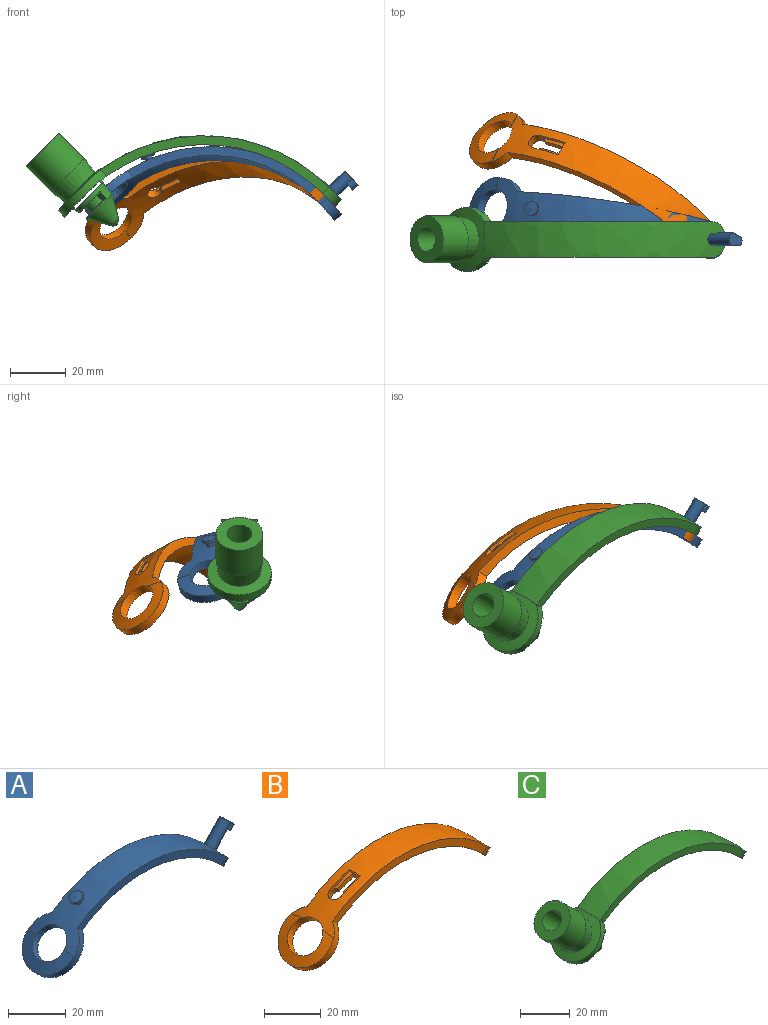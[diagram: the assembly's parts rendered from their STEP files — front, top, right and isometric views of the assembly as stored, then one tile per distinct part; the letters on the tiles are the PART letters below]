
ASSEMBLY  parts=3 mates=1
PART A: 20 faces, bbox 97.4x31.8x29.1 mm
  f0: sphere r=56.9mm, area 1169.8mm2, adj f1,f2,f3,f4,f9,f10,f11,f12
  f1: plane 72.67x18.82mm, normal (0,1,0), area 245.3mm2, adj f0,f8,f9,f11
  f2: plane 72.67x18.82mm, normal (0,-1,0), area 245.3mm2, adj f0,f8,f9,f11
  f3: cone r=40.93mm half-angle=46deg, axis (-1,0,0), area 1.2mm2, adj f0,f5,f9,f10
  f4: cone r=40.93mm half-angle=46deg, axis (-1,0,0), area 1.2mm2, adj f0,f5,f9,f10
  f5: sphere r=57.15mm, area 135.1mm2, adj f3,f4,f9,f10
  f6: sphere r=53.98mm, area 247.2mm2, adj f7,f9,f10
  f7: cone r=43.67mm half-angle=54deg, axis (-1,0,0), area 4.2mm2, adj f6,f8,f9
  f8: sphere r=53.72mm, area 1032.4mm2, adj f1,f2,f7,f9,f11
  f9: cylinder r=11.43mm len=22.86mm, axis (0.71,0,-0.71), area 184.7mm2, adj f0,f1,f2,f3,f4,f5,f6,f7
  f10: cone r=6.43mm half-angle=6.9deg, axis (-0.71,0,0.71), area 128.2mm2, adj f0,f3,f4,f5,f6
  f11: cylinder r=6.35mm len=12.7mm, axis (-0.71,0,-0.71), area 63.8mm2, adj f0,f1,f2,f8
  f12: cylinder r=2.28mm len=11.12mm, axis (0.68,0,0.73), area 149.3mm2, adj f0,f13,f14,f15
  f13: plane 5x4.69mm, normal (0.68,0,0.73), area 23.8mm2, adj f12,f14
  f14: cylinder r=1.78mm len=3.78mm, axis (0.68,0,0.73), area 19.8mm2, adj f12,f13,f15
  f15: plane 3.56x2.05mm, normal (-0.68,0,-0.73), area 7.4mm2, adj f12,f14
  f16: plane 5.08x4.53mm, normal (0.45,0,-0.89), area 15.2mm2, adj f17,f19
  f17: cylinder r=1.27mm len=3.13mm, axis (-0.45,0,0.89), area 15.3mm2, adj f0,f16
  f18: cone r=2.54mm half-angle=85deg, axis (0.45,0,-0.89), area 20.3mm2, adj f19
  f19: cylinder r=2.54mm len=5.08mm, axis (-0.45,0,0.89), area 16.7mm2, adj f16,f18
PART B: 21 faces, bbox 96.8x31.8x29.9 mm
  f0: sphere r=56.9mm, area 1144.5mm2, adj f2,f3,f6,f7,f8,f9,f14,f15
  f1: sphere r=60.07mm, area 1134.9mm2, adj f6,f7,f11,f12,f14,f15,f16,f17
  f2: plane 7.97x4.53mm, normal (0,1,0), area 14.9mm2, adj f0,f4,f17,f20
  f3: plane 7.97x4.53mm, normal (0,-1,0), area 14.9mm2, adj f0,f5,f17,f20
  f4: cylinder r=58.8mm len=9.51mm, axis (0,-1,0), area 10.9mm2, adj f2,f17,f19,f20
  f5: cylinder r=58.8mm len=9.51mm, axis (0,-1,0), area 10.9mm2, adj f3,f17,f18,f20
  f6: plane 77.22x19.75mm, normal (0,1,0), area 261.2mm2, adj f0,f1,f14,f16
  f7: plane 77.22x19.75mm, normal (0,-1,0), area 261.2mm2, adj f0,f1,f14,f16
  f8: cone r=40.93mm half-angle=46deg, axis (-1,0,0), area 1.2mm2, adj f0,f10,f14,f15
  f9: cone r=40.93mm half-angle=46deg, axis (-1,0,0), area 1.2mm2, adj f0,f10,f14,f15
  f10: sphere r=57.15mm, area 135.1mm2, adj f8,f9,f14,f15
  f11: cone r=46.21mm half-angle=50deg, axis (-1,0,0), area 1.4mm2, adj f1,f13,f14,f15
  f12: cone r=46.21mm half-angle=50deg, axis (-1,0,0), area 1.4mm2, adj f1,f13,f14,f15
  f13: sphere r=60.32mm, area 166.4mm2, adj f11,f12,f14,f15
  f14: cylinder r=11.43mm len=22.86mm, axis (0.71,0,-0.71), area 191.3mm2, adj f0,f1,f6,f7,f8,f9,f10,f11
  f15: cone r=6.43mm half-angle=6.9deg, axis (-0.71,0,0.71), area 143.2mm2, adj f0,f1,f8,f9,f10,f11,f12,f13
  f16: cylinder r=6.35mm len=12.7mm, axis (-0.71,0,-0.71), area 63.7mm2, adj f0,f1,f6,f7
  f17: plane 5.6x3.07mm, normal (-0.96,0,-0.29), area 12.8mm2, adj f0,f1,f2,f3,f4,f5,f18,f19
  f18: plane 10.08x5.01mm, normal (0,-1,0), area 12.5mm2, adj f1,f5,f17,f20
  f19: plane 10.08x5.01mm, normal (0,1,0), area 12.5mm2, adj f1,f4,f17,f20
  f20: cylinder r=2.79mm len=6.02mm, axis (0.45,0,-0.89), area 38.7mm2, adj f0,f1,f2,f3,f4,f5,f18,f19
PART C: 36 faces, bbox 112.8x26.4x33.2 mm
  f0: sphere r=60.07mm, area 1159.1mm2, adj f1,f2,f6,f9,f10,f11,f26,f27
  f1: cone r=6.43mm half-angle=6.9deg, axis (-0.71,0,0.71), area 134.6mm2, adj f0,f2,f3,f4,f5,f17,f21,f24
  f2: cone r=6.43mm half-angle=6.9deg, axis (-0.71,0,0.71), area 0.2mm2, adj f0,f1,f33
  f3: cone r=46.21mm half-angle=50deg, axis (-1,0,0), area 0.2mm2, adj f1,f5,f30
  f4: cone r=46.21mm half-angle=50deg, axis (-1,0,0), area 0.2mm2, adj f1,f5,f30
  f5: sphere r=60.32mm, area 100.4mm2, adj f1,f3,f4,f6,f29,f30,f32
  f6: cylinder r=11.43mm len=22.86mm, axis (0.71,0,-0.71), area 177.8mm2, adj f0,f5,f10,f11,f13,f29,f30,f32
  f7: cone r=3.13mm half-angle=3.1deg, axis (-0.71,0,0.71), area 530mm2, adj f14,f30
  f8: sphere r=63.25mm, area 1174.1mm2, adj f9,f10,f11,f12,f26,f27
  f9: cylinder r=2.28mm len=5mm, axis (0.73,0,0.68), area 34mm2, adj f0,f8,f27
  f10: plane 81.94x20.69mm, normal (0,1,0), area 277.1mm2, adj f0,f6,f8,f12,f13,f26
  f11: plane 81.94x20.69mm, normal (0,-1,0), area 277.1mm2, adj f0,f6,f8,f12,f13,f26
  f12: cone r=51.37mm half-angle=54deg, axis (-1,0,0), area 3.2mm2, adj f8,f10,f11,f13
  f13: sphere r=63.5mm, area 217.3mm2, adj f6,f10,f11,f12,f16
  f14: plane 16.76x11.85mm, normal (-0.71,0,0.71), area 160.1mm2, adj f7,f15
  f15: cylinder r=8.38mm len=20.83mm, axis (0.71,0,-0.71), area 668.9mm2, adj f14,f16
  f16: cone r=6.43mm half-angle=6.9deg, axis (-0.71,0,0.71), area 310.5mm2, adj f13,f15
  f17: cone r=1.8mm half-angle=30.4deg, axis (-0.71,0,0.71), area 236.6mm2, adj f1,f18,f22
  f18: sphere r=2.09mm, area 13.5mm2, adj f17
  f19: cone r=3.81mm half-angle=3.1deg, axis (-0.71,0,0.71), area 47.6mm2, adj f20,f23,f24,f25
  f20: sphere r=56.9mm, area 56.4mm2, adj f19,f21,f24,f25
  f21: torus R=6.4mm, axis (-0.71,0,0.71), area 23.1mm2, adj f1,f20,f24,f25
  f22: torus R=5.93mm, axis (-0.71,0,0.71), area 22mm2, adj f17,f23,f24,f25
  f23: sphere r=53.98mm, area 49.2mm2, adj f19,f22,f24,f25
  f24: plane 3.67x3.54mm, normal (-0.58,0.57,-0.58), area 8.7mm2, adj f1,f19,f20,f21,f22,f23
  f25: plane 3.67x3.54mm, normal (-0.58,-0.57,-0.58), area 8.7mm2, adj f1,f19,f20,f21,f22,f23
  f26: cylinder r=6.35mm len=12.7mm, axis (-0.71,0,-0.71), area 63.7mm2, adj f0,f8,f10,f11
  f27: cylinder r=2.03mm len=4.64mm, axis (-0.73,0,-0.68), area 28.5mm2, adj f0,f8,f9
  f28: plane 5.92x0.91mm, normal (0.71,0,0.71), area 7mm2, adj f1,f30,f31
  f29: plane 3.62x0.32mm, normal (0.71,0,0.71), area 0.8mm2, adj f5,f6,f30
  f30: plane 22.88x9.36mm, normal (0.71,0,-0.71), area 212.6mm2, adj f1,f3,f4,f5,f6,f7,f28,f29
  f31: plane 14.16x9.34mm, normal (-0.71,0,0.71), area 123.3mm2, adj f1,f28,f33,f35
  f32: plane 3.62x0.32mm, normal (0.71,0,0.71), area 0.8mm2, adj f5,f6,f30
  f33: plane 18.67x0.91mm, normal (-0.71,0,-0.71), area 11.2mm2, adj f0,f1,f2,f6,f30,f31
  f34: cone r=0mm half-angle=28.2deg, axis (-0.71,0,0.71), area 65.4mm2, adj f35
  f35: cone r=3.13mm half-angle=3.1deg, axis (-0.71,0,0.71), area 1mm2, adj f31,f34
PLACE A rot(axis=(-0.67,0.31,-0.67),11.9deg) t=(-12.29,-5.62,7.76)mm
PLACE B rot(axis=(-0.71,0,-0.71),37.8deg) t=(-14.61,-5.62,5.59)mm
PLACE C t=(-14.61,-5.62,5.59)mm fixed
MATE revolute C.f9 <-> A.f12  axis (0.73,0,0.68) through (29.18,-5.62,46.64)mm
